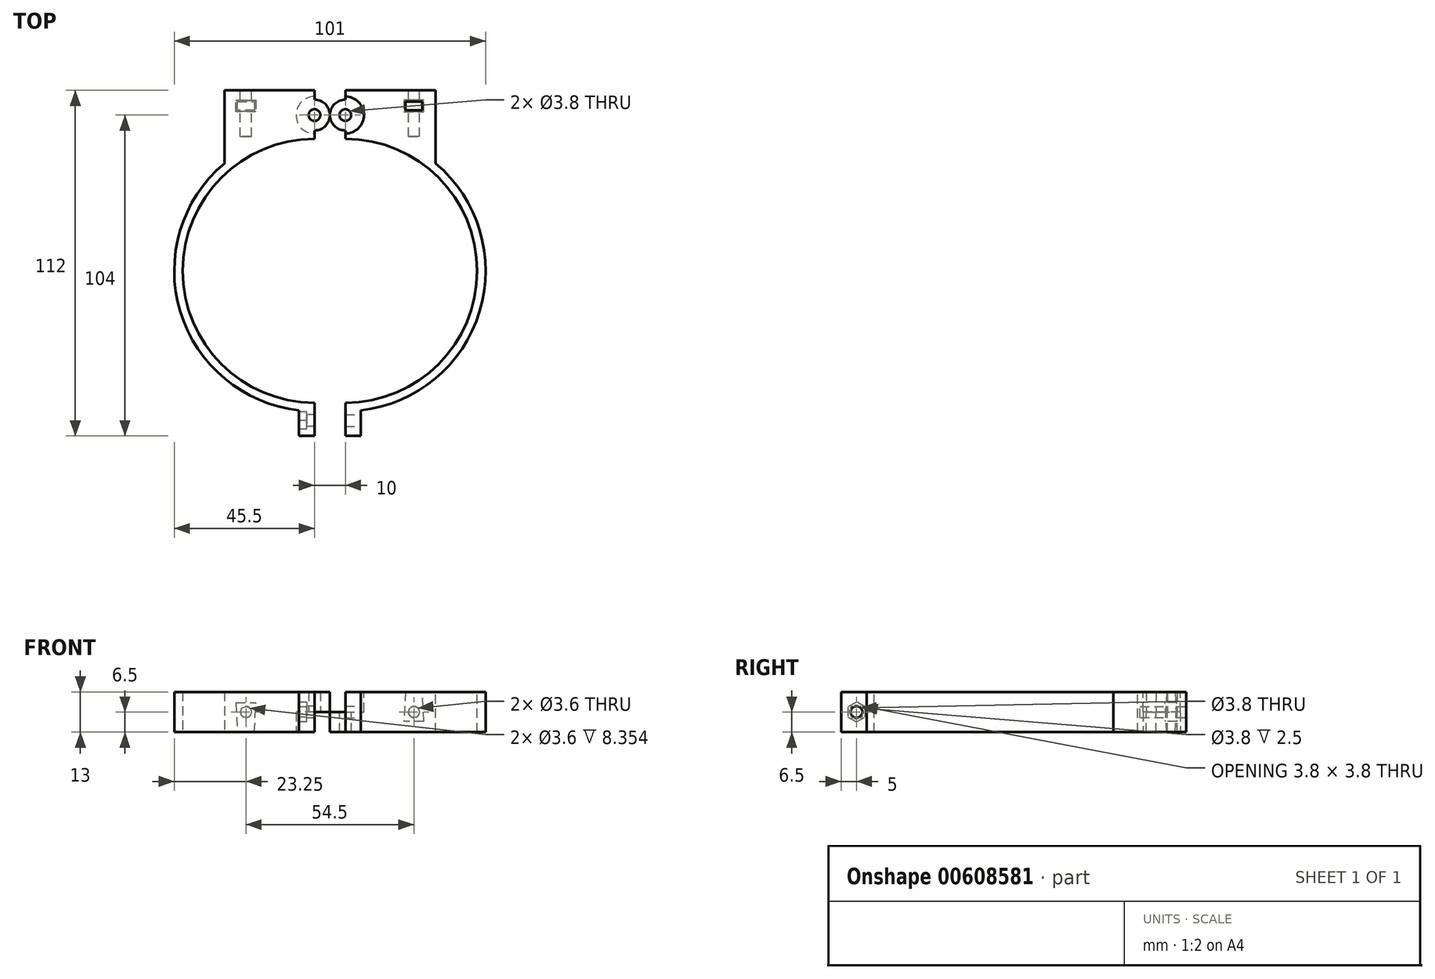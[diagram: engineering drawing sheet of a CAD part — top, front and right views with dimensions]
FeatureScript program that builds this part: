
annotation { "Feature Type Name" : "Feature", "Feature Type Description" : "" }
export const myFeature = defineFeature(function(context is Context, id is Id, definition is map)
    precondition{}
    {
        {
            assignVariable(context, id + "F0", {"name" : "width", "anyValue" : 13});
        }
        {
            var Q0;
            Q0=qCreatedBy(makeId("Top.planeOp"),FACE);
            var sketch = newSketch(context, id + "F1", { "sketchPlane" : qUnion([Q0])});
            skArc(sketch, "E0", {"start": v(0, 42.75) * mm, "mid": v(-42.75, 0) * mm, "end": v(0, -42.75) * mm});
            skArc(sketch, "E1", {"start": v(0, 45.5) * mm, "mid": v(-45.5, 0) * mm, "end": v(0, -45.5) * mm});
            skLineSegment(sketch, "E2", {"start": v(0, 45.5) * mm, "end": v(0, 42.75) * mm});
            skPoint(sketch, "E3", {"position": v(0, -42.75) * mm});
            skPoint(sketch, "E4", {"position": v(0, -45.5) * mm});
            skPoint(sketch, "E5", {"position": v(0, 42.75) * mm});
            skPoint(sketch, "E6", {"position": v(0, 45.5) * mm});
            skLineSegment(sketch, "E7.trimOffspring", {"start": v(0, -42.75) * mm, "end": v(0, -45.5) * mm});
            skLineSegment(sketch, "E8", {"start": v(0, -45.5) * mm, "end": v(0, -53.5) * mm});
            skLineSegment(sketch, "E9", {"start": v(0, -53.5) * mm, "end": v(-5, -53.5) * mm});
            skLineSegment(sketch, "E10", {"start": v(-5, -53.5) * mm, "end": v(-5, -45.22) * mm});
            skLineSegment(sketch, "E11", {"start": v(0, -45.5) * mm, "end": v(-5, -45.5) * mm});
            skLineSegment(sketch, "E12", {"start": v(0, 42.75) * mm, "end": v(0, 58.25) * mm, "construction": true});
            skCircle(sketch, "E13", {"center": v(0, 50.5) * mm, "radius": 1.9 * mm});
            skLineSegment(sketch, "E14", {"start": v(0, 45.5) * mm, "end": v(0, 48.6) * mm});
            skLineSegment(sketch, "E15", {"start": v(0, 58.5) * mm, "end": v(-29.25, 58.5) * mm});
            skLineSegment(sketch, "E16", {"start": v(-29.25, 58.5) * mm, "end": v(-29.25, 34.85) * mm});
            skCircle(sketch, "E17", {"center": v(0, 50.5) * mm, "radius": 5 * mm});
            skLineSegment(sketch, "E18", {"start": v(0, 58.5) * mm, "end": v(0, 55.5) * mm});
            skLineSegment(sketch, "E19", {"start": v(0, 45.5) * mm, "end": v(-29.25, 45.5) * mm, "construction": true});
            skArc(sketch, "E20", {"start": v(0, 56.5) * mm, "mid": v(-6, 50.5) * mm, "end": v(0, 44.5) * mm});
            skSolve(sketch);
        }
        {
            var Q0;
            Q0=makeQuery(id+"F1.imprint","IMPRINT",FACE,{"disambiguationData":[TD([[makeQuery(id+"F1.imprint","IMPRINT",EDGE,{"derivedFrom":sQuery(id+"F1.wireOp",EDGE,"E0")}),-1.0]])]});
            var Q1;
            {var subQ0=sQuery(id+"F1.wireOp",EDGE,"E11");Q1=makeQuery(id+"F1.imprint","IMPRINT",FACE,{"disambiguationData":[TD([[makeQuery(id+"F1.imprint","IMPRINT",EDGE,{"derivedFrom":subQ0}),-1.0]])]});}
            var Q2;
            Q2=makeQuery(id+"F1.imprint","IMPRINT",FACE,{"disambiguationData":[TD([[makeQuery(id+"F1.imprint","IMPRINT",EDGE,{"derivedFrom":sQuery(id+"F1.wireOp",EDGE,"E8")}),-1.0]])]});
            var Q3;
            {var subQ0=sQuery(id+"F1.wireOp",EDGE,"SyQSAPXu-U66S-BtnH-oFi6-cjTa1mpKTWbp");Q3=makeQuery(id+"F1.imprint","IMPRINT",FACE,{"disambiguationData":[TD([[makeQuery(id+"F1.imprint","IMPRINT",EDGE,{"derivedFrom":subQ0}),1.0]])]});}
            var Q4;
            {var subQ1=sQuery(id+"F1.wireOp",EDGE,"E14");Q4=makeQuery(id+"F1.imprint","IMPRINT",FACE,{"disambiguationData":[TD([[makeQuery(id+"F1.imprint","IMPRINT",EDGE,{"derivedFrom":subQ1}),1.0]])]});}
            var Q5;
            Q5=makeQuery(id+"F1.imprint","IMPRINT",FACE,{"disambiguationData":[TD([[makeQuery(id+"F1.imprint","IMPRINT",EDGE,{"derivedFrom":sQuery(id+"F1.wireOp",EDGE,"E15")}),1.0]])]});
            extrude(context, id + "F2", {"entities" : qUnion([Q0, Q1, Q2, Q3, Q4, Q5]), "endBound" : BoundingType.SYMMETRIC, "depth" : (getVariable(context, 'width')) * mm, "offsetDistance" : 25 * mm});
        }
        {
            var Q0;
            Q0=makeQuery(id+"F1.imprint","IMPRINT",FACE,{"disambiguationData":[TD([[makeQuery(id+"F1.imprint","IMPRINT",EDGE,{"derivedFrom":sQuery(id+"F1.wireOp",EDGE,"E13")}),-1.0]])]});
            var Q1;
            {var subQ0=sQuery(id+"F1.wireOp",EDGE,"E17");var subQ5=sQuery(id+"F1.wireOp",EDGE,"E18");var subQ6=makeQuery(id+"F1.imprint","INTERSECT",VERTEX,{"derivedFrom":[subQ0,subQ5]});Q1=makeQuery(id+"F1.imprint","IMPRINT",FACE,{"disambiguationData":[TD([[makeQuery(id+"F1.imprint","IMPRINT",EDGE,{"disambiguationData":[TD([[subQ6,1.0]])],"derivedFrom":subQ5}),-1.0]])]});}
            var Q2;
            {var subQ0=sQuery(id+"F1.wireOp",EDGE,"E2");var subQ3=sQuery(id+"F1.wireOp",EDGE,"E20");var subQ5=makeQuery(id+"F1.imprint","INTERSECT",VERTEX,{"derivedFrom":[subQ0,subQ3]});Q2=makeQuery(id+"F1.imprint","IMPRINT",FACE,{"disambiguationData":[TD([[makeQuery(id+"F1.imprint","IMPRINT",EDGE,{"disambiguationData":[TD([[subQ5,1.0]])],"derivedFrom":subQ3}),1.0]])]});}
            var Q3;
            Q3=makeQuery(id+"F2.opExtrude","CAP_FACE",FACE,{"disambiguationData":[OSD([sQuery(id+"F1.wireOp",EDGE,"E0"),sQuery(id+"F1.wireOp",EDGE,"E1"),sQuery(id+"F1.wireOp",EDGE,"E2"),sQuery(id+"F1.wireOp",EDGE,"E7.trimOffspring"),sQuery(id+"F1.wireOp",EDGE,"E8"),sQuery(id+"F1.wireOp",EDGE,"E9"),sQuery(id+"F1.wireOp",EDGE,"E10"),sQuery(id+"F1.wireOp",EDGE,"E14"),sQuery(id+"F1.wireOp",EDGE,"E15"),sQuery(id+"F1.wireOp",EDGE,"E16"),sQuery(id+"F1.wireOp",EDGE,"E17"),sQuery(id+"F1.wireOp",EDGE,"E18")])],"isStart":false});
            extrude(context, id + "F3", {"entities" : qUnion([Q0, Q1, Q2]), "operationType" : NewBodyOperationType.ADD, "endBound" : BoundingType.UP_TO_SURFACE, "depth" : 4 * mm, "endBoundEntityFace" : qUnion([Q3]), "offsetDistance" : 25 * mm});
        }
        {
            var Q0;
            Q0=makeQuery(id+"F2.opExtrude","SWEPT_FACE",FACE,{"disambiguationData":[OSD([sQuery(id+"F1.wireOp",EDGE,"E10")])]});
            var sketch = newSketch(context, id + "F4", { "sketchPlane" : qUnion([Q0])});
            skLineSegment(sketch, "E21", {"start": v(53.5, 0) * mm, "end": v(45.22, 0) * mm, "construction": true});
            skCircle(sketch, "E22", {"center": v(48.5, 0) * mm, "radius": 1.9 * mm});
            skSolve(sketch);
        }
        {
            var Q0;
            Q0=makeQuery(id+"F4.imprint","IMPRINT",FACE,{"disambiguationData":[TD([[makeQuery(id+"F4.imprint","IMPRINT",EDGE,{"derivedFrom":sQuery(id+"F4.wireOp",EDGE,"E22")}),1.0]])]});
            extrude(context, id + "F5", {"entities" : qUnion([Q0]), "operationType" : NewBodyOperationType.REMOVE, "endBound" : BoundingType.THROUGH_ALL, "oppositeDirection" : true, "depth" : 25 * mm, "offsetDistance" : 25 * mm});
        }
        {
            var Q0;
            Q0=makeQuery(id+"F2.opExtrude","SWEPT_FACE",FACE,{"disambiguationData":[OSD([sQuery(id+"F1.wireOp",EDGE,"E15")])]});
            var sketch = newSketch(context, id + "F6", { "sketchPlane" : qUnion([Q0])});
            skCircle(sketch, "E23", {"center": v(22.25, 0) * mm, "radius": 1.8 * mm});
            skLineSegment(sketch, "E24", {"start": v(22.25, 0) * mm, "end": v(22.25, -6.5) * mm, "construction": true});
            skSolve(sketch);
        }
        {
            var Q0;
            Q0=makeQuery(id+"F6.imprint","IMPRINT",FACE,{"disambiguationData":[TD([[makeQuery(id+"F6.imprint","IMPRINT",EDGE,{"derivedFrom":sQuery(id+"F6.wireOp",EDGE,"E23")}),1.0]])]});
            extrude(context, id + "F7", {"entities" : qUnion([Q0]), "operationType" : NewBodyOperationType.REMOVE, "oppositeDirection" : true, "depth" : 15 * mm, "offsetDistance" : 25 * mm});
        }
        {
            var Q0;
            Q0=makeQuery(id+"F2.opExtrude","CAP_FACE",FACE,{"disambiguationData":[OSD([sQuery(id+"F1.wireOp",EDGE,"E0"),sQuery(id+"F1.wireOp",EDGE,"E1"),sQuery(id+"F1.wireOp",EDGE,"E2"),sQuery(id+"F1.wireOp",EDGE,"E7.trimOffspring"),sQuery(id+"F1.wireOp",EDGE,"E8"),sQuery(id+"F1.wireOp",EDGE,"E9"),sQuery(id+"F1.wireOp",EDGE,"E10"),sQuery(id+"F1.wireOp",EDGE,"E14"),sQuery(id+"F1.wireOp",EDGE,"E15"),sQuery(id+"F1.wireOp",EDGE,"E16"),sQuery(id+"F1.wireOp",EDGE,"E17"),sQuery(id+"F1.wireOp",EDGE,"E18")])],"isStart":true});
            var sketch = newSketch(context, id + "F8", { "sketchPlane" : qUnion([Q0])});
            skLineSegment(sketch, "E25", {"start": v(-22.25, -58.5) * mm, "end": v(-22.25, -45.39) * mm, "construction": true});
            skLineSegment(sketch, "E26.bottom", {"start": v(-19.5, -54.9) * mm, "end": v(-25, -54.9) * mm});
            skLineSegment(sketch, "E26.top", {"start": v(-19.5, -52.1) * mm, "end": v(-25, -52.1) * mm});
            skLineSegment(sketch, "E26.left", {"start": v(-19.5, -54.9) * mm, "end": v(-19.5, -52.1) * mm});
            skLineSegment(sketch, "E26.right", {"start": v(-25, -54.9) * mm, "end": v(-25, -52.1) * mm});
            skPoint(sketch, "E26.middle", {"position": v(-22.25, -53.5) * mm});
            skSolve(sketch);
        }
        {
            var Q0;
            Q0=makeQuery(id+"F8.imprint","IMPRINT",FACE,{"disambiguationData":[TD([[makeQuery(id+"F8.imprint","IMPRINT",EDGE,{"derivedFrom":sQuery(id+"F8.wireOp",EDGE,"E26.bottom")}),-1.0]])]});
            extrude(context, id + "F9", {"entities" : qUnion([Q0]), "operationType" : NewBodyOperationType.REMOVE, "oppositeDirection" : true, "depth" : (getVariable(context, 'width') / 2 + 3) * mm, "offsetDistance" : 25 * mm, "hasDraft" : true, "draftAngle" : 3 * degree});
        }
        {
            var Q0;
            Q0=makeQuery(id+"F2.opExtrude","SWEPT_BODY",BODY,{"disambiguationData":[OSD([sQuery(id+"F1.wireOp",EDGE,"E0"),sQuery(id+"F1.wireOp",EDGE,"E1"),sQuery(id+"F1.wireOp",EDGE,"E2"),sQuery(id+"F1.wireOp",EDGE,"E7.trimOffspring"),sQuery(id+"F1.wireOp",EDGE,"E8"),sQuery(id+"F1.wireOp",EDGE,"E9"),sQuery(id+"F1.wireOp",EDGE,"E10"),sQuery(id+"F1.wireOp",EDGE,"E15"),sQuery(id+"F1.wireOp",EDGE,"E16"),sQuery(id+"F1.wireOp",EDGE,"E17"),sQuery(id+"F1.wireOp",EDGE,"E18")])]});
            transform(context, id + "F10", {"entities" : qUnion([Q0]), "transformType" : TransformType.TRANSLATION_3D, "dx" : 10 * mm, "dy" : 0 * mm, "dz" : 0 * mm, "makeCopy" : true});
        }
        {
            var Q0;
            Q0=makeQuery(id+"F10.opPattern","COPY",BODY,{"derivedFrom":makeQuery(id+"F2.opExtrude","SWEPT_BODY",BODY,{"disambiguationData":[OSD([sQuery(id+"F1.wireOp",EDGE,"E0"),sQuery(id+"F1.wireOp",EDGE,"E1"),sQuery(id+"F1.wireOp",EDGE,"E2"),sQuery(id+"F1.wireOp",EDGE,"E7.trimOffspring"),sQuery(id+"F1.wireOp",EDGE,"E8"),sQuery(id+"F1.wireOp",EDGE,"E9"),sQuery(id+"F1.wireOp",EDGE,"E10"),sQuery(id+"F1.wireOp",EDGE,"E15"),sQuery(id+"F1.wireOp",EDGE,"E16"),sQuery(id+"F1.wireOp",EDGE,"E17"),sQuery(id+"F1.wireOp",EDGE,"E18")])]}),"instanceName":"1"});
            var Q1;
            Q1=makeQuery(id+"F10.opPattern","COPY",EDGE,{"derivedFrom":makeQuery(id+"F3.opExtrude","CAP_EDGE",EDGE,{"disambiguationData":[OSD([sQuery(id+"F1.wireOp",EDGE,"E2")])],"isStart":true}),"instanceName":"1"});
            transform(context, id + "F11", {"entities" : qUnion([Q0]), "transformType" : TransformType.ROTATION, "transformAxis" : qUnion([Q1]), "angle" : 180 * degree, "makeCopy" : false});
        }
        {
            var Q0;
            Q0=makeQuery(id+"F2.opExtrude","SWEPT_FACE",FACE,{"disambiguationData":[OSD([sQuery(id+"F1.wireOp",EDGE,"E10")])]});
            var sketch = newSketch(context, id + "F12", { "sketchPlane" : qUnion([Q0])});
            skLineSegment(sketch, "E27", {"start": v(53.5, 0) * mm, "end": v(45.22, 0) * mm, "construction": true});
            skCircle(sketch, "E28.cCircle", {"center": v(48.5, 0) * mm, "radius": 2.8 * mm, "construction": true});
            skPoint(sketch, "E28.cCircle.perimeterSnap0", {"position": v(49.36, 0) * mm});
            skLineSegment(sketch, "E28.0", {"start": v(45.7, -1.62) * mm, "end": v(45.7, 1.62) * mm});
            skLineSegment(sketch, "E28.1", {"start": v(45.7, 1.62) * mm, "end": v(48.5, 3.23) * mm});
            skLineSegment(sketch, "E28.2", {"start": v(48.5, 3.23) * mm, "end": v(51.3, 1.62) * mm});
            skLineSegment(sketch, "E28.3", {"start": v(51.3, 1.62) * mm, "end": v(51.3, -1.62) * mm});
            skLineSegment(sketch, "E28.4", {"start": v(51.3, -1.62) * mm, "end": v(48.5, -3.23) * mm});
            skLineSegment(sketch, "E28.5", {"start": v(48.5, -3.23) * mm, "end": v(45.7, -1.62) * mm});
            skPoint(sketch, "E28.0.midPoint", {"position": v(45.7, 0) * mm});
            skPoint(sketch, "E28.0.midPoint.positionSnap0", {"position": v(49.36, 0) * mm});
            skSolve(sketch);
        }
        {
            var Q0;
            Q0=makeQuery(id+"F12.imprint","IMPRINT",FACE,{"disambiguationData":[TD([[makeQuery(id+"F12.imprint","IMPRINT",EDGE,{"derivedFrom":sQuery(id+"F12.wireOp",EDGE,"E28.0")}),-1.0]])]});
            extrude(context, id + "F13", {"entities" : qUnion([Q0]), "operationType" : NewBodyOperationType.REMOVE, "oppositeDirection" : true, "depth" : 2.5 * mm, "offsetDistance" : 25 * mm});
        }
    });
